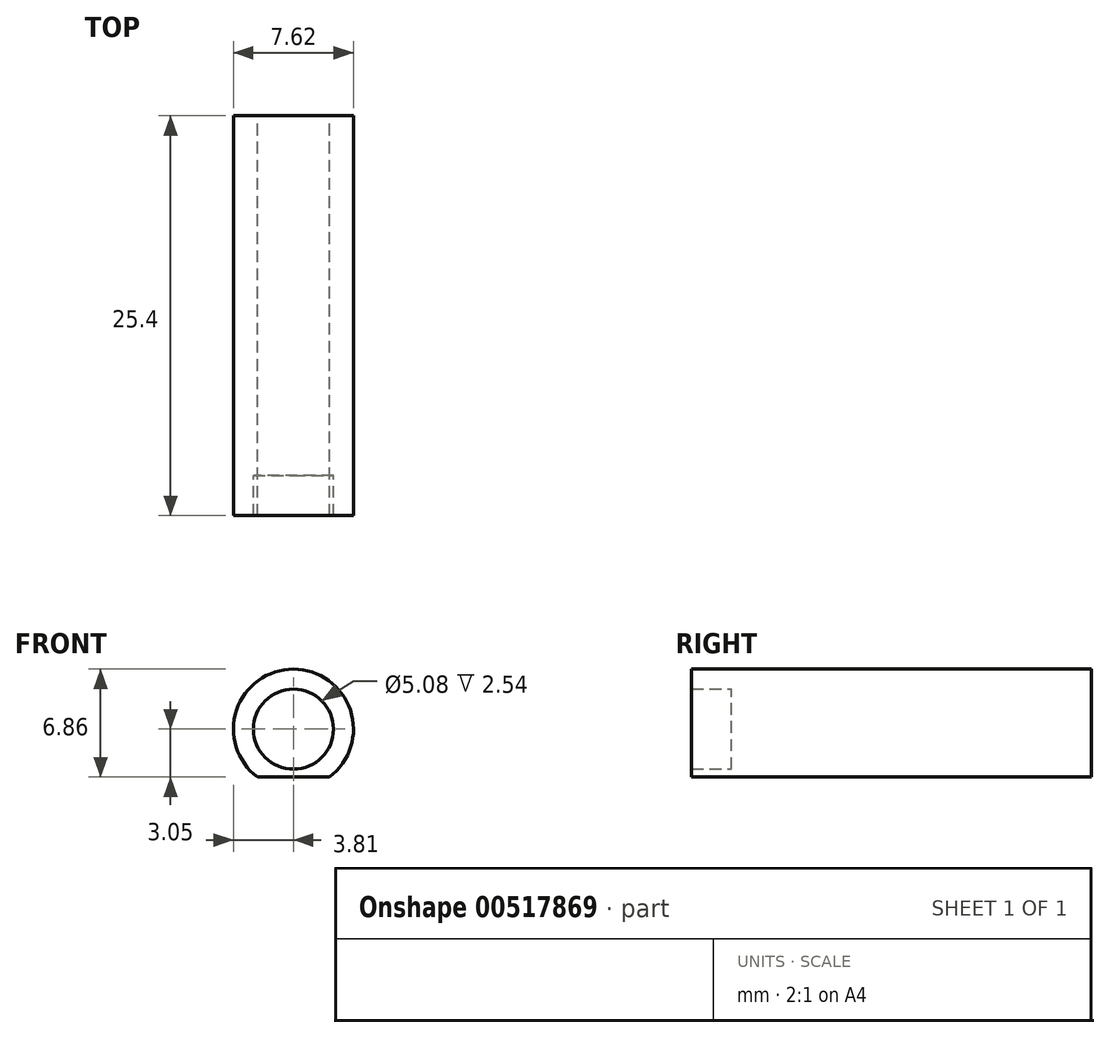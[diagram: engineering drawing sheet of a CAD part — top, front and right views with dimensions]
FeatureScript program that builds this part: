
annotation { "Feature Type Name" : "Feature", "Feature Type Description" : "" }
export const myFeature = defineFeature(function(context is Context, id is Id, definition is map)
    precondition{}
    {
        {
            var Q0;
            Q0=qCreatedBy(makeId("Front.planeOp"),FACE);
            var sketch = newSketch(context, id + "F0", { "sketchPlane" : qUnion([Q0])});
            skCircle(sketch, "E0", {"center": v(0, 0) * mm, "radius": 3.81 * mm});
            skCircle(sketch, "E1", {"center": v(0, 0) * mm, "radius": 2.54 * mm});
            skLineSegment(sketch, "E2", {"start": v(-2.29, -3.05) * mm, "end": v(2.29, -3.05) * mm});
            skSolve(sketch);
        }
        {
            var Q0;
            Q0=makeQuery(id+"F0.imprint","IMPRINT",FACE,{"disambiguationData":[TD([[makeQuery(id+"F0.imprint","IMPRINT",EDGE,{"derivedFrom":sQuery(id+"F0.wireOp",EDGE,"E1")}),-1.0]])]});
            extrude(context, id + "F1", {"entities" : qUnion([Q0]), "depth" : 25.4 * mm, "offsetDistance" : 25.4 * mm});
        }
        {
            var Q0;
            Q0=makeQuery(id+"F0.imprint","IMPRINT",FACE,{"disambiguationData":[TD([[makeQuery(id+"F0.imprint","IMPRINT",EDGE,{"derivedFrom":sQuery(id+"F0.wireOp",EDGE,"E1")}),1.0]])]});
            extrude(context, id + "F2", {"entities" : qUnion([Q0]), "operationType" : NewBodyOperationType.ADD, "depth" : 22.86 * mm, "offsetDistance" : 25.4 * mm});
        }
    });
